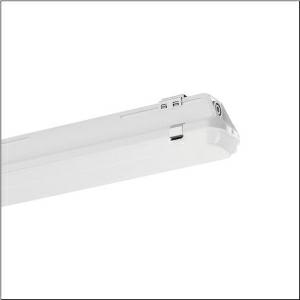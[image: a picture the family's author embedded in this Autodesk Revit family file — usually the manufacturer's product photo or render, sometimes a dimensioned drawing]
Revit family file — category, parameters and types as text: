
# Revit family: monsun_r__21_51fb20dl440k_f82c
name_source: partatom
category: Lighting Fixtures
units: mm (PartAtom-declared; Revit-internal decimal feet)

## family parameters
Cut with Voids When Loaded = No
Host = Face
Light Source = No
Part Type = Normal
Room Calculation Point = No
Round Connector Dimension = Use Diameter
Shared = No

## types (1)
- --- (1 x LED, 4320 lm, 26.6 W, 4000K)
    Apparent Load = 27 VA
    CIE Flux Codes = 45 75 93 94 100
    Color Rendering = 80
    Color Temperature = 4000K
    Default Elevation = 1800 mm
    Description = Monsun® 21, damp-proof luminaire, chain hanger, primary optical cover: enclosure, of PC, light emission: direct distribution, primary light characteristic: symmetric, installation type: suspended mounting, surface-mounted, horizontal mounting, vertical mounting, LED, rated luminous flux: 4.320lm, luminous efficacy: 162lm/W, light colour: 840, colour temperature: 4000K, control gear: DALI 2, with terminal, 5-pole, max. 2.5mm², mains connection: 220..240V, AC, 50/60Hz, rated input power: 27W, housing, of glass-fibre reinforced plastic, uncoated, bright grey, incl. chain hanger, length: 1.299mm, width: 90mm, height: 88mm, clip for enclosure, of stainless steel (V2A), ceiling mounting element, of stainless steel (V2A), chain hanger, of stainless steel (V2A), protection rating (complete): IP66, insulation class (complete): insulation class I (protective earthing), certification: CE, ENEC, VDE, UKCA, protection symbol: D, impact resistance: IK08, permissible operating ambient temperature: -25..+35°C, standard: EN 50419, EN 60598-2-1, corresponds to IFS (International Featured Standards) requirements for safety and quality in the food industry, for indoor or canopied outdoor use, no direct snow, no direct sun, no direct rain, LABS conformity tested according to VDMA 24364:2018-05, contact your sales advisor before using the luminaires in applications with unclear chemical exposure, large temperature fluctuations or condensation-forming humidity, packaging unit: 1 piece
    Height = 88 mm
    Lamp = 1 x LED
    Lamp Light Flux = 4320 lm
    Lamp Power = 26.6 W
    Lamp count = 1
    Length = 1299 mm
    Luminous efficacy = 162 lm/W
    Manufacturer = Siteco
    ModVariant = No
    Model = 51FB20DL440K
    Mounting Place = Ceiling
    Mounting Type = Surface mounted
    Number of Poles = 1
    OnlyDefault = Yes
    Power Factor = 1
    Product Name = Monsun® 21
    Product group = damp-proof luminaire
    ProductGroupID = 300
    Protection Class = Protection class I
    Protection Degree = IP 66
    RLX_Detail_Level = 1
    RLX_Emergency_Light_Flux = 0 lm
    RLX_Emergency_Type = 0
    RLX_Emergency_Type_DB = No
    RlxData = <blob elided: 93557 chars, md5=02e5a8ac>
    Socket = socket
    Standby Power = 0 W
    System Light Flux = 4320 lm
    System Power = 27 W
    Type Comments = factory setting: luminous flux: 100 % | dim-lin: 254 | 182 mA
    Type Image = l_1319656.jpg
    URL = http://relux.com
    VarID = @adj_022364
    Voltage = 0 V
    Weight = 0.00 kg
    Width = 90 mm

## geometry (parser evidence)
native form markers: Blend x4, Sweep x12
no freeform markers — native parametric forms only
